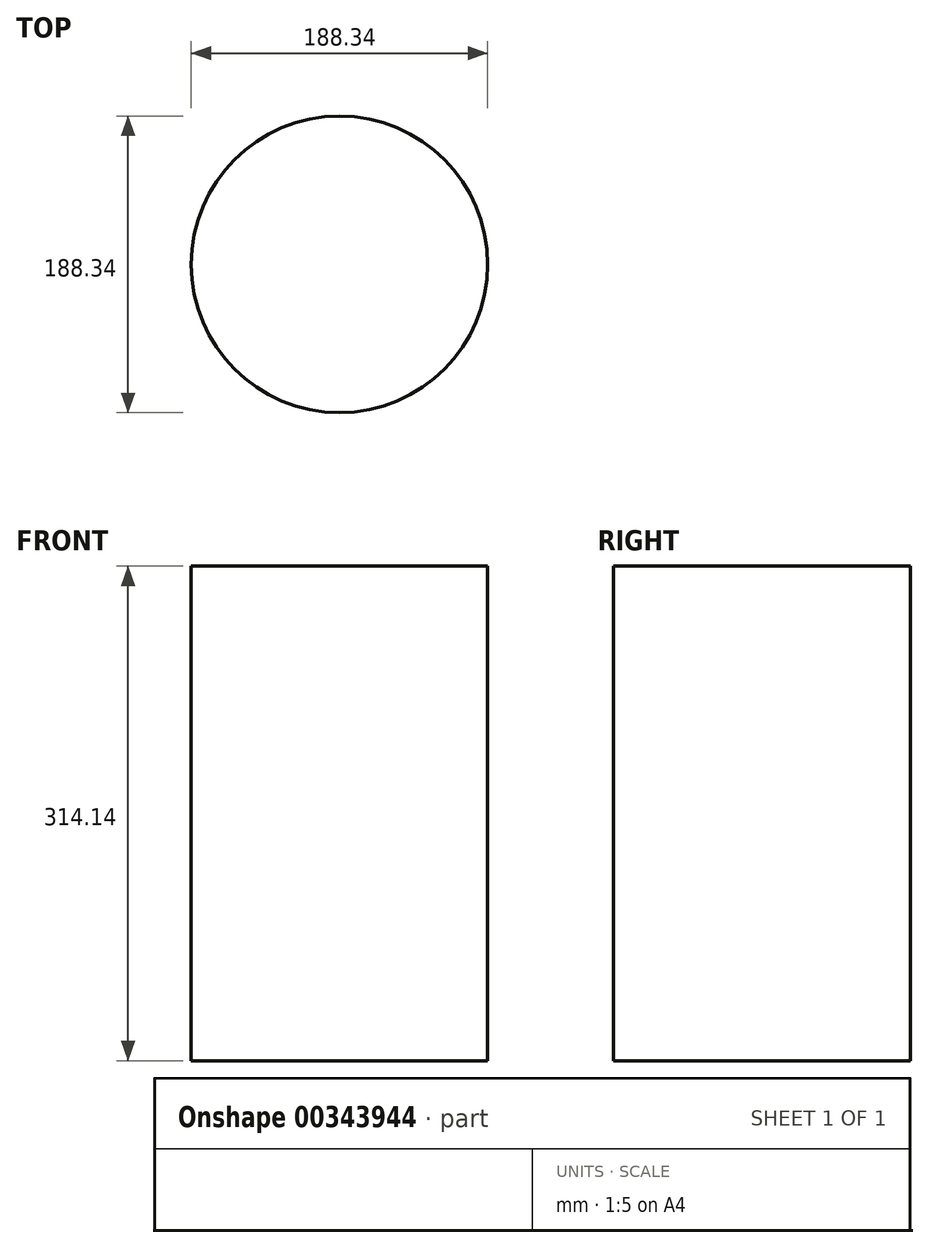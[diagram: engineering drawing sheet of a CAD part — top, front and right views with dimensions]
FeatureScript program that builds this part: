
annotation { "Feature Type Name" : "Feature", "Feature Type Description" : "" }
export const myFeature = defineFeature(function(context is Context, id is Id, definition is map)
    precondition{}
    {
        {
            var Q0;
            Q0=qCreatedBy(makeId("Top.planeOp"),FACE);
            var sketch = newSketch(context, id + "F0", { "sketchPlane" : qUnion([Q0])});
            skCircle(sketch, "E0", {"center": v(0, 0) * mm, "radius": 94.17 * mm});
            skSolve(sketch);
        }
        {
            var Q0;
            Q0=makeQuery(id+"F0.imprint","IMPRINT",FACE,{"disambiguationData":[TD([[makeQuery(id+"F0.imprint","IMPRINT",EDGE,{"derivedFrom":sQuery(id+"F0.wireOp",EDGE,"E0")}),1.0]])]});
            extrude(context, id + "F1", {"entities" : qUnion([Q0]), "depth" : 314.14 * mm});
        }
    });
